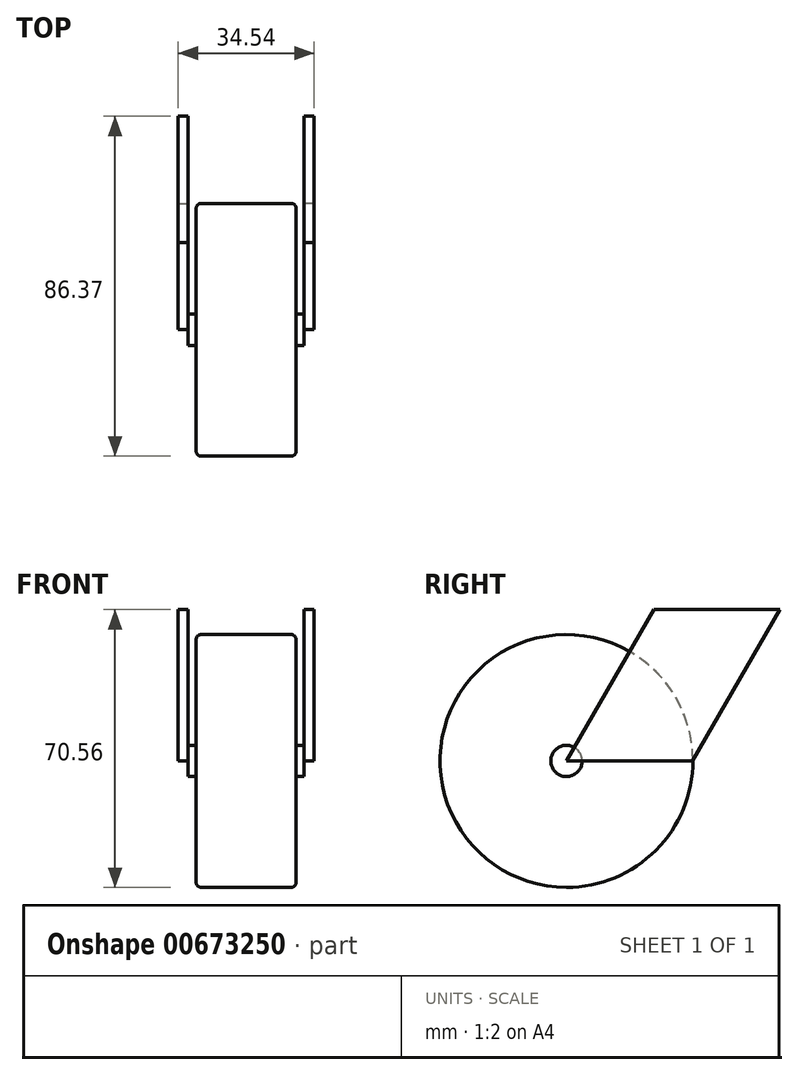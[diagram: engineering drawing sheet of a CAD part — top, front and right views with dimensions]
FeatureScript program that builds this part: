
annotation { "Feature Type Name" : "Feature", "Feature Type Description" : "" }
export const myFeature = defineFeature(function(context is Context, id is Id, definition is map)
    precondition{}
    {
        {
            var Q0;
            Q0=qCreatedBy(makeId("Right.planeOp"),FACE);
            var sketch = newSketch(context, id + "F0", { "sketchPlane" : qUnion([Q0])});
            skCircle(sketch, "E0", {"center": v(0, 0) * mm, "radius": 32.11 * mm});
            skSolve(sketch);
        }
        {
            var Q0;
            Q0=makeQuery(id+"F0.imprint","IMPRINT",FACE,{"disambiguationData":[TD([[makeQuery(id+"F0.imprint","IMPRINT",EDGE,{"derivedFrom":sQuery(id+"F0.wireOp",EDGE,"E0")}),1.0]])]});
            extrude(context, id + "F1", {"entities" : qUnion([Q0]), "depth" : 25.4 * mm, "offsetDistance" : 25.4 * mm});
        }
        {
            var Q0;
            Q0=makeQuery(id+"F1.opExtrude","CAP_EDGE",EDGE,{"disambiguationData":[OSD([sQuery(id+"F0.wireOp",EDGE,"E0")])],"isStart":false});
            fillet(context, id + "F2", {"entities" : qUnion([Q0]), "radius" : 1.27 * mm, "tangentPropagation" : true, "allowEdgeOverflow" : false});
        }
        {
            var Q0;
            Q0=makeQuery(id+"F1.opExtrude","CAP_EDGE",EDGE,{"disambiguationData":[OSD([sQuery(id+"F0.wireOp",EDGE,"E0")])],"isStart":true});
            fillet(context, id + "F3", {"entities" : qUnion([Q0]), "radius" : 1.27 * mm, "tangentPropagation" : true, "allowEdgeOverflow" : false});
        }
        {
            var Q0;
            Q0=makeQuery(id+"F1.opExtrude","CAP_FACE",FACE,{"disambiguationData":[OSD([sQuery(id+"F0.wireOp",EDGE,"E0")])],"isStart":false});
            var sketch = newSketch(context, id + "F4", { "sketchPlane" : qUnion([Q0])});
            skCircle(sketch, "E1", {"center": v(0, 0) * mm, "radius": 3.98 * mm});
            skSolve(sketch);
        }
        {
            var Q0;
            Q0 = qSketchRegion(id + "F4", true);
            extrude(context, id + "F5", {"entities" : qUnion([Q0]), "operationType" : NewBodyOperationType.ADD, "depth" : 2.03 * mm, "offsetDistance" : 25.4 * mm});
        }
        {
            var Q0;
            Q0=makeQuery(id+"F1.opExtrude","CAP_FACE",FACE,{"disambiguationData":[OSD([sQuery(id+"F0.wireOp",EDGE,"E0")])],"isStart":true});
            var sketch = newSketch(context, id + "F6", { "sketchPlane" : qUnion([Q0])});
            skSolve(sketch);
        }
        {
            var Q0;
            {var subQ0=sQuery(id+"F0.wireOp",EDGE,"E0");Q0=makeQuery(id+"F6.imprint","IMPRINT",FACE,{"disambiguationData":[TD([[makeQuery(id+"F6.imprint","IMPRINT",EDGE,{"derivedFrom":makeQuery(id+"F3.opFillet","BLEND_EDGE",EDGE,{"blendedFrom":[makeQuery(id+"F1.opExtrude","CAP_EDGE",EDGE,{"disambiguationData":[OSD([subQ0])],"isStart":true}),makeQuery(id+"F1.opExtrude","CAP_FACE",FACE,{"disambiguationData":[OSD([subQ0])],"isStart":true})],"blendedInto":[makeQuery(id+"F1.opExtrude","CAP_FACE",FACE,{"disambiguationData":[OSD([subQ0])],"isStart":true})]})}),1.0]])]});}
            var sketch = newSketch(context, id + "F7", { "sketchPlane" : qUnion([Q0])});
            skCircle(sketch, "E2", {"center": v(0, 0) * mm, "radius": 3.98 * mm});
            skSolve(sketch);
        }
        {
            var Q0;
            Q0 = qSketchRegion(id + "F7", true);
            extrude(context, id + "F8", {"entities" : qUnion([Q0]), "operationType" : NewBodyOperationType.ADD, "depth" : 2.03 * mm, "offsetDistance" : 25.4 * mm});
        }
        {
            var Q0;
            Q0=makeQuery(id+"F8.opExtrude","CAP_FACE",FACE,{"disambiguationData":[OSD([sQuery(id+"F7.wireOp",EDGE,"E2")])],"isStart":false});
            var sketch = newSketch(context, id + "F9", { "sketchPlane" : qUnion([Q0])});
            skLineSegment(sketch, "E3", {"start": v(0, 0) * mm, "end": v(-22.2, 38.45) * mm});
            skLineSegment(sketch, "E4", {"start": v(-22.2, 38.45) * mm, "end": v(-54.26, 38.45) * mm});
            skLineSegment(sketch, "E5", {"start": v(-54.26, 38.45) * mm, "end": v(-32.06, 0) * mm});
            skLineSegment(sketch, "E6", {"start": v(-32.06, 0) * mm, "end": v(0, 0) * mm});
            skSolve(sketch);
        }
        {
            var Q0;
            {var subQ4=sQuery(id+"F9.wireOp",EDGE,"E4");Q0=makeQuery(id+"F9.imprint","IMPRINT",FACE,{"disambiguationData":[TD([[makeQuery(id+"F9.imprint","IMPRINT",EDGE,{"derivedFrom":subQ4}),1.0]])]});}
            var Q1;
            {var subQ0=sQuery(id+"F9.wireOp",EDGE,"E6");var subQ1=sQuery(id+"F9.wireOp",EDGE,"E3");var subQ2=makeQuery(id+"F9.imprint","INTERSECT",VERTEX,{"derivedFrom":[subQ1,subQ0]});Q1=makeQuery(id+"F9.imprint","IMPRINT",FACE,{"disambiguationData":[TD([[makeQuery(id+"F9.imprint","IMPRINT",EDGE,{"disambiguationData":[TD([[subQ2,-1.0]])],"derivedFrom":subQ1}),1.0]])]});}
            extrude(context, id + "F10", {"entities" : qUnion([Q0, Q1]), "operationType" : NewBodyOperationType.ADD, "depth" : 2.54 * mm, "offsetDistance" : 25.4 * mm});
        }
        {
            var Q0;
            Q0=makeQuery(id+"F5.opExtrude","CAP_FACE",FACE,{"disambiguationData":[OSD([sQuery(id+"F4.wireOp",EDGE,"E1")])],"isStart":false});
            var sketch = newSketch(context, id + "F11", { "sketchPlane" : qUnion([Q0])});
            skLineSegment(sketch, "E7.0", {"start": v(54.26, 38.45) * mm, "end": v(32.06, 0) * mm});
            skLineSegment(sketch, "E7.1", {"start": v(22.2, 38.45) * mm, "end": v(54.26, 38.45) * mm});
            skLineSegment(sketch, "E7.2", {"start": v(0, 0) * mm, "end": v(22.2, 38.45) * mm});
            skLineSegment(sketch, "E7.3", {"start": v(32.06, 0) * mm, "end": v(0, 0) * mm});
            skSolve(sketch);
        }
        {
            var Q0;
            Q0 = qSketchRegion(id + "F11", true);
            extrude(context, id + "F12", {"entities" : qUnion([Q0]), "operationType" : NewBodyOperationType.ADD, "depth" : 2.54 * mm, "offsetDistance" : 25.4 * mm});
        }
    });
